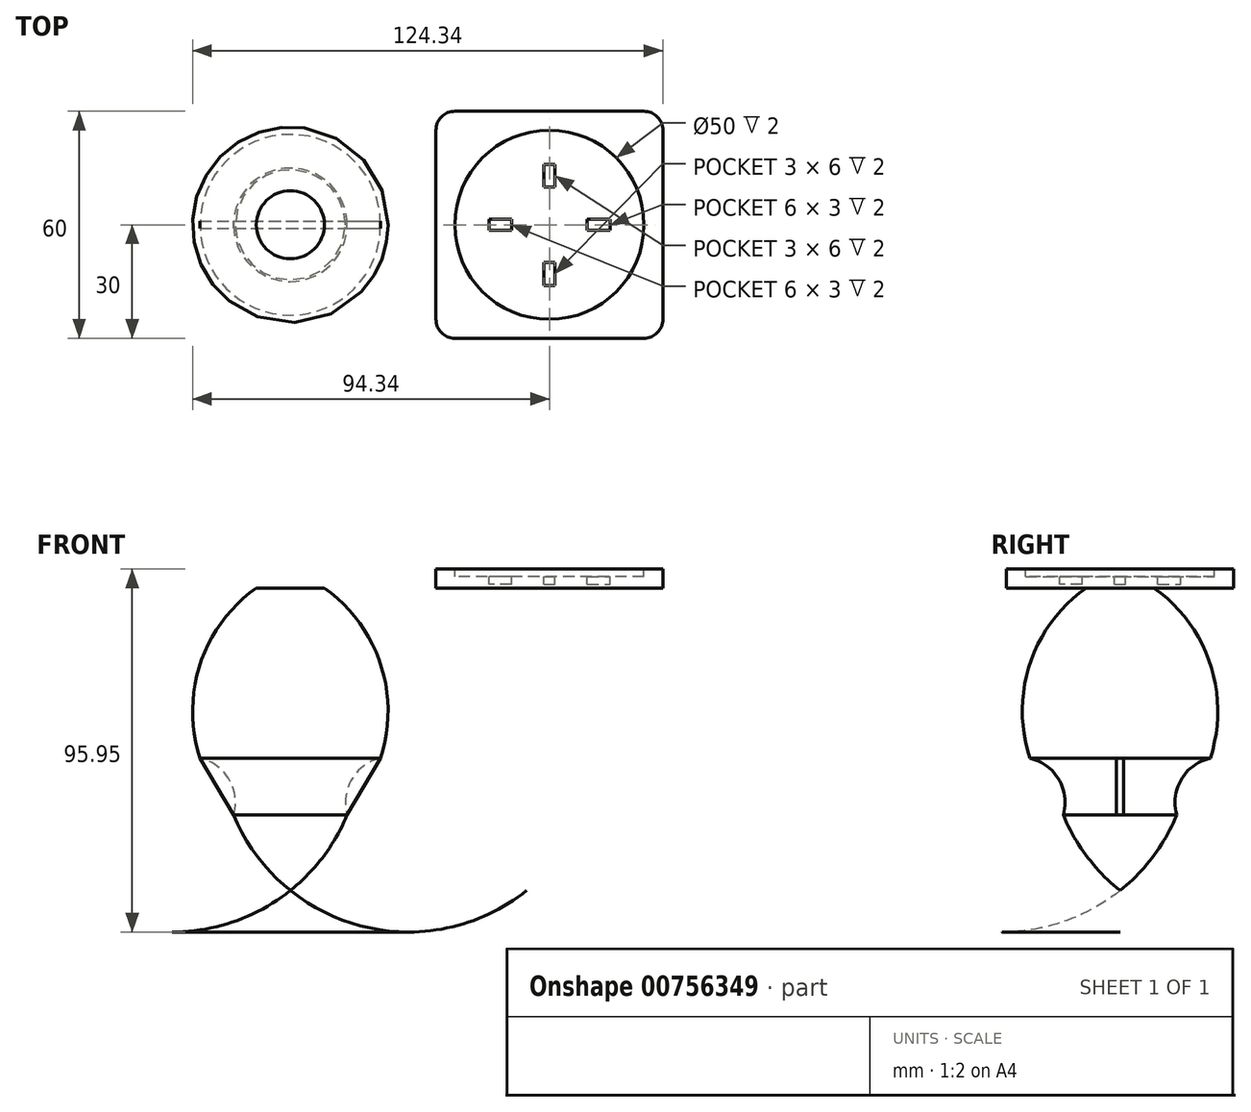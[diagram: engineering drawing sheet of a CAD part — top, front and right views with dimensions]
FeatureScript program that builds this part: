
annotation { "Feature Type Name" : "Feature", "Feature Type Description" : "" }
export const myFeature = defineFeature(function(context is Context, id is Id, definition is map)
    precondition{}
    {
        {
            var Q0;
            Q0=qCreatedBy(makeId("Top.planeOp"),FACE);
            var sketch = newSketch(context, id + "F0", { "sketchPlane" : qUnion([Q0])});
            skLineSegment(sketch, "E0.bottom", {"start": v(-30, 30) * mm, "end": v(30, 30) * mm});
            skLineSegment(sketch, "E0.top", {"start": v(-30, -30) * mm, "end": v(30, -30) * mm});
            skLineSegment(sketch, "E0.left", {"start": v(-30, 30) * mm, "end": v(-30, -30) * mm});
            skLineSegment(sketch, "E0.right", {"start": v(30, 30) * mm, "end": v(30, -30) * mm});
            skPoint(sketch, "E0.middle", {"position": v(0, 0) * mm});
            skSolve(sketch);
        }
        {
            var Q0;
            Q0=makeQuery(id+"F0.imprint","IMPRINT",FACE,{"disambiguationData":[TD([[makeQuery(id+"F0.imprint","IMPRINT",EDGE,{"derivedFrom":sQuery(id+"F0.wireOp",EDGE,"E0.bottom")}),-1.0]])]});
            extrude(context, id + "F1", {"entities" : qUnion([Q0]), "depth" : 5 * mm, "offsetDistance" : 25 * mm});
        }
        {
            var Q0;
            Q0=makeQuery(id+"F1.opExtrude","CAP_FACE",FACE,{"disambiguationData":[OSD([sQuery(id+"F0.wireOp",EDGE,"E0.bottom"),sQuery(id+"F0.wireOp",EDGE,"E0.top"),sQuery(id+"F0.wireOp",EDGE,"E0.left"),sQuery(id+"F0.wireOp",EDGE,"E0.right")])],"isStart":false});
            var sketch = newSketch(context, id + "F2", { "sketchPlane" : qUnion([Q0])});
            skCircle(sketch, "E1", {"center": v(0, 0) * mm, "radius": 25 * mm});
            skSolve(sketch);
        }
        {
            var Q0;
            Q0=makeQuery(id+"F2.imprint","IMPRINT",FACE,{"disambiguationData":[TD([[makeQuery(id+"F2.imprint","IMPRINT",EDGE,{"derivedFrom":sQuery(id+"F2.wireOp",EDGE,"E1")}),1.0]])]});
            extrude(context, id + "F3", {"entities" : qUnion([Q0]), "operationType" : NewBodyOperationType.REMOVE, "oppositeDirection" : true, "depth" : 2 * mm, "offsetDistance" : 25 * mm});
        }
        {
            var Q0;
            Q0=makeQuery(id+"F1.opExtrude","SWEPT_EDGE",EDGE,{"disambiguationData":[OSD([sQuery(id+"F0.wireOp",EDGE,"E0.top"),sQuery(id+"F0.wireOp",EDGE,"E0.left")])]});
            var Q1;
            Q1=makeQuery(id+"F1.opExtrude","SWEPT_EDGE",EDGE,{"disambiguationData":[OSD([sQuery(id+"F0.wireOp",EDGE,"E0.top"),sQuery(id+"F0.wireOp",EDGE,"E0.right")])]});
            var Q2;
            Q2=makeQuery(id+"F1.opExtrude","SWEPT_EDGE",EDGE,{"disambiguationData":[OSD([sQuery(id+"F0.wireOp",EDGE,"E0.bottom"),sQuery(id+"F0.wireOp",EDGE,"E0.right")])]});
            var Q3;
            Q3=makeQuery(id+"F1.opExtrude","SWEPT_EDGE",EDGE,{"disambiguationData":[OSD([sQuery(id+"F0.wireOp",EDGE,"E0.bottom"),sQuery(id+"F0.wireOp",EDGE,"E0.left")])]});
            fillet(context, id + "F4", {"entities" : qUnion([Q0, Q1, Q2, Q3]), "radius" : 5 * mm, "tangentPropagation" : true, "allowEdgeOverflow" : false});
        }
        {
            var Q0;
            Q0=makeQuery(id+"F3.boolean.opBoolean","COPY",FACE,{"derivedFrom":makeQuery(id+"F3.opExtrude","CAP_FACE",FACE,{"disambiguationData":[OSD([sQuery(id+"F2.wireOp",EDGE,"E1")])],"isStart":false})});
            var sketch = newSketch(context, id + "F5", { "sketchPlane" : qUnion([Q0])});
            skLineSegment(sketch, "E2.bottom", {"start": v(1.5, 10) * mm, "end": v(-1.5, 10) * mm});
            skLineSegment(sketch, "E2.top", {"start": v(1.5, 16) * mm, "end": v(-1.5, 16) * mm});
            skLineSegment(sketch, "E2.left", {"start": v(1.5, 10) * mm, "end": v(1.5, 16) * mm});
            skLineSegment(sketch, "E2.right", {"start": v(-1.5, 10) * mm, "end": v(-1.5, 16) * mm});
            skPoint(sketch, "E2.middle", {"position": v(0, 13) * mm});
            skLineSegment(sketch, "E3.1.0", {"start": v(-10, -1.5) * mm, "end": v(-16, -1.5) * mm});
            skLineSegment(sketch, "E3.1.1", {"start": v(-10, 1.5) * mm, "end": v(-16, 1.5) * mm});
            skLineSegment(sketch, "E3.1.2", {"start": v(-16, 1.5) * mm, "end": v(-16, -1.5) * mm});
            skLineSegment(sketch, "E3.1.3", {"start": v(-10, 1.5) * mm, "end": v(-10, -1.5) * mm});
            skPoint(sketch, "E3.1.4", {"position": v(-13, 0) * mm});
            skLineSegment(sketch, "E3.2.0", {"start": v(1.5, -10) * mm, "end": v(1.5, -16) * mm});
            skLineSegment(sketch, "E3.2.1", {"start": v(-1.5, -10) * mm, "end": v(-1.5, -16) * mm});
            skLineSegment(sketch, "E3.2.2", {"start": v(-1.5, -16) * mm, "end": v(1.5, -16) * mm});
            skLineSegment(sketch, "E3.2.3", {"start": v(-1.5, -10) * mm, "end": v(1.5, -10) * mm});
            skPoint(sketch, "E3.2.4", {"position": v(0, -13) * mm});
            skLineSegment(sketch, "E3.3.0", {"start": v(10, 1.5) * mm, "end": v(16, 1.5) * mm});
            skLineSegment(sketch, "E3.3.1", {"start": v(10, -1.5) * mm, "end": v(16, -1.5) * mm});
            skLineSegment(sketch, "E3.3.2", {"start": v(16, -1.5) * mm, "end": v(16, 1.5) * mm});
            skLineSegment(sketch, "E3.3.3", {"start": v(10, -1.5) * mm, "end": v(10, 1.5) * mm});
            skPoint(sketch, "E3.3.4", {"position": v(13, 0) * mm});
            skPoint(sketch, "E3.center", {"position": v(0, 0) * mm});
            skSolve(sketch);
        }
        {
            var Q0;
            Q0=makeQuery(id+"F5.imprint","IMPRINT",FACE,{"disambiguationData":[TD([[makeQuery(id+"F5.imprint","IMPRINT",EDGE,{"derivedFrom":sQuery(id+"F5.wireOp",EDGE,"E3.1.0")}),-1.0]])]});
            var Q1;
            Q1=makeQuery(id+"F5.imprint","IMPRINT",FACE,{"disambiguationData":[TD([[makeQuery(id+"F5.imprint","IMPRINT",EDGE,{"derivedFrom":sQuery(id+"F5.wireOp",EDGE,"E2.bottom")}),-1.0]])]});
            var Q2;
            Q2=makeQuery(id+"F5.imprint","IMPRINT",FACE,{"disambiguationData":[TD([[makeQuery(id+"F5.imprint","IMPRINT",EDGE,{"derivedFrom":sQuery(id+"F5.wireOp",EDGE,"E3.3.0")}),-1.0]])]});
            var Q3;
            Q3=makeQuery(id+"F5.imprint","IMPRINT",FACE,{"disambiguationData":[TD([[makeQuery(id+"F5.imprint","IMPRINT",EDGE,{"derivedFrom":sQuery(id+"F5.wireOp",EDGE,"E3.2.0")}),-1.0]])]});
            extrude(context, id + "F6", {"entities" : qUnion([Q0, Q1, Q2, Q3]), "operationType" : NewBodyOperationType.REMOVE, "oppositeDirection" : true, "depth" : 2 * mm, "offsetDistance" : 25 * mm});
        }
        {
            var Q0;
            Q0=qCreatedBy(makeId("Front.planeOp"),FACE);
            var sketch = newSketch(context, id + "F7", { "sketchPlane" : qUnion([Q0])});
            skLineSegment(sketch, "E4", {"start": v(-68.5, 0) * mm, "end": v(-68.5, -80) * mm});
            skLineSegment(sketch, "E5", {"start": v(-68.5, 0) * mm, "end": v(-59.5, 0) * mm});
            skLineSegment(sketch, "E6", {"start": v(-68.5, -60) * mm, "end": v(-53.5, -60) * mm});
            skLineSegment(sketch, "E7", {"start": v(-68.5, -45) * mm, "end": v(-44.62, -45) * mm});
            skArc(sketch, "E8", {"start": v(-44.62, -45) * mm, "mid": v(-44.68, -20.06) * mm, "end": v(-59.5, 0) * mm});
            skArc(sketch, "E9", {"start": v(-68.5, -80) * mm, "mid": v(-59.73, -70.95) * mm, "end": v(-53.5, -60) * mm});
            skArc(sketch, "E10", {"start": v(-44.62, -45) * mm, "mid": v(-52.29, -50.59) * mm, "end": v(-53.5, -60) * mm});
            skLineSegment(sketch, "E11", {"start": v(-68.5, 0) * mm, "end": v(-68.5, -2) * mm});
            skLineSegment(sketch, "E12", {"start": v(-68.5, -2) * mm, "end": v(-61.5, -2) * mm});
            skLineSegment(sketch, "E13", {"start": v(-61.5, -2) * mm, "end": v(-61.5, 0) * mm});
            skSolve(sketch);
        }
        {
            var Q0;
            Q0 = qSketchRegion(id + "F7", true);
            var Q1;
            Q1 = qSketchRegion(id + "F9", true);
            var Q2;
            Q2 = qSketchRegion(id + "F11", true);
            var Q3;
            Q3=sQuery(id+"F7.wireOp",EDGE,"E4");
            revolve(context, id + "F8", {"surfaceOperationType" : NewSurfaceOperationType.NEW, "entities" : qUnion([Q0, Q1, Q2]), "axis" : qUnion([Q3]), "revolveType" : RevolveType.FULL});
        }
        {
            var Q0;
            Q0=qCreatedBy(makeId("Front.planeOp"),FACE);
            var sketch = newSketch(context, id + "F9", { "sketchPlane" : qUnion([Q0])});
            skLineSegment(sketch, "E14.0", {"start": v(-92.38, -45) * mm, "end": v(-44.62, -45) * mm});
            skLineSegment(sketch, "E15.0", {"start": v(-83.5, -60) * mm, "end": v(-53.5, -60) * mm});
            skLineSegment(sketch, "E16", {"start": v(-92.38, -45) * mm, "end": v(-83.5, -60) * mm});
            skLineSegment(sketch, "E17", {"start": v(-53.5, -60) * mm, "end": v(-44.62, -45) * mm});
            skSolve(sketch);
        }
        {
            var Q0;
            Q0 = qSketchRegion(id + "F9", true);
            extrude(context, id + "F10", {"entities" : qUnion([Q0]), "endBound" : BoundingType.SYMMETRIC, "depth" : 2 * mm, "offsetDistance" : 25 * mm});
        }
    });
